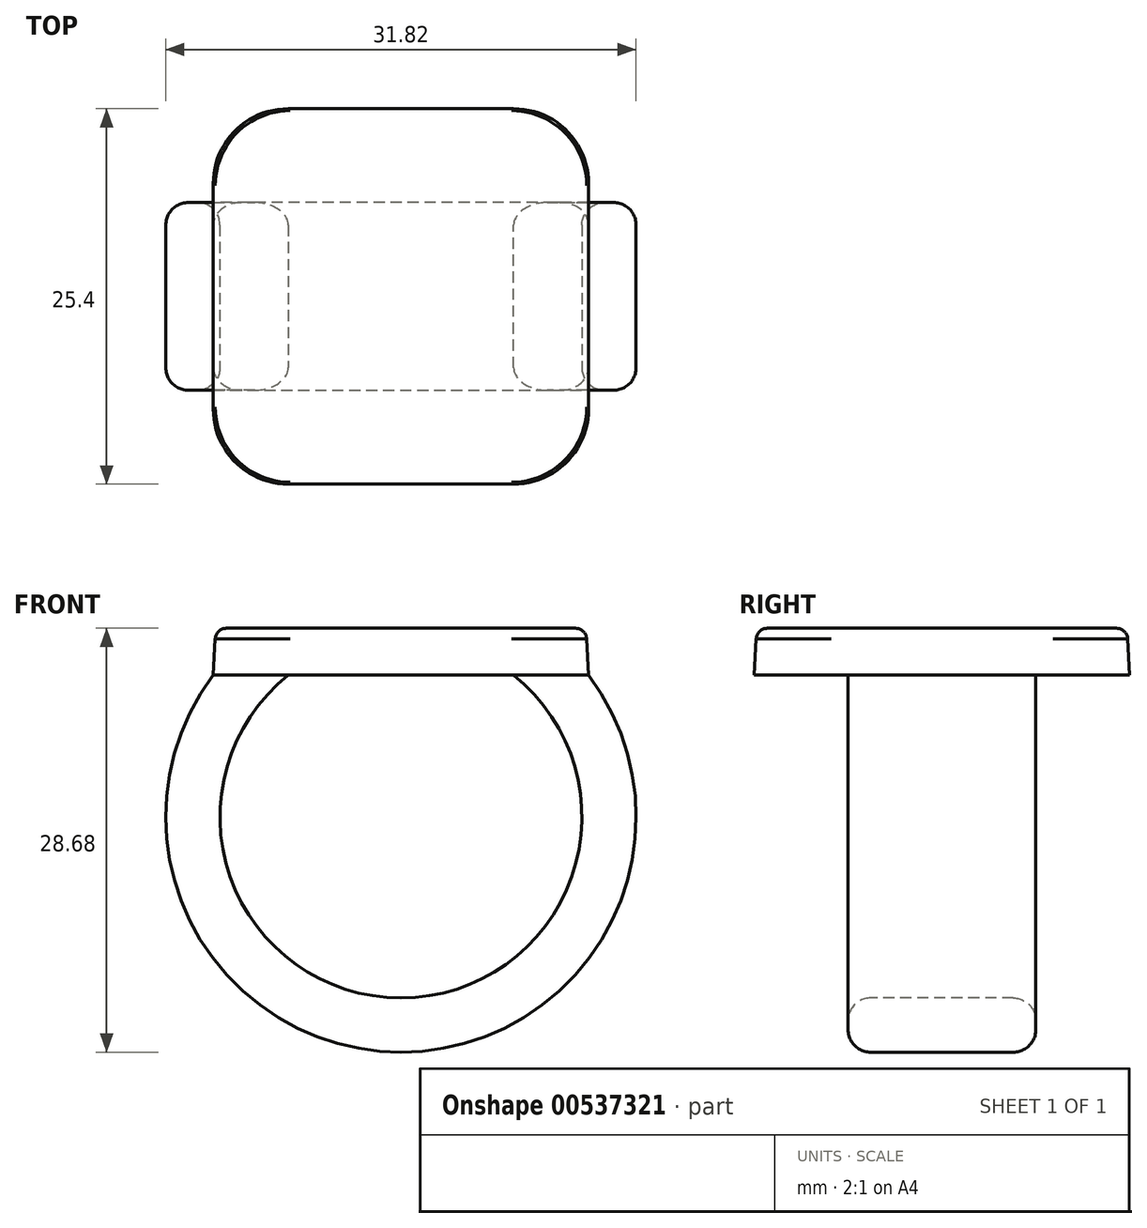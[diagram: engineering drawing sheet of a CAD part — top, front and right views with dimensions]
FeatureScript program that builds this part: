
annotation { "Feature Type Name" : "Feature", "Feature Type Description" : "" }
export const myFeature = defineFeature(function(context is Context, id is Id, definition is map)
    precondition{}
    {
        {
            var Q0;
            Q0=qCreatedBy(makeId("Top.planeOp"),FACE);
            var sketch = newSketch(context, id + "F0", { "sketchPlane" : qUnion([Q0])});
            skLineSegment(sketch, "E0.bottom", {"start": v(12.7, -12.7) * mm, "end": v(-12.7, -12.7) * mm});
            skLineSegment(sketch, "E0.top", {"start": v(12.7, 12.7) * mm, "end": v(-12.7, 12.7) * mm});
            skLineSegment(sketch, "E0.left", {"start": v(12.7, -12.7) * mm, "end": v(12.7, 12.7) * mm});
            skLineSegment(sketch, "E0.right", {"start": v(-12.7, -12.7) * mm, "end": v(-12.7, 12.7) * mm});
            skPoint(sketch, "E0.middle", {"position": v(0, 0) * mm});
            skSolve(sketch);
        }
        {
            var Q0;
            Q0 = qSketchRegion(id + "F0", true);
            extrude(context, id + "F1", {"entities" : qUnion([Q0]), "depth" : 3.17 * mm, "offsetDistance" : 25.4 * mm, "hasDraft" : true, "draftAngle" : 3 * degree, "draftPullDirection" : true});
        }
        {
            var Q0;
            Q0=qCreatedBy(makeId("Front.planeOp"),FACE);
            var sketch = newSketch(context, id + "F2", { "sketchPlane" : qUnion([Q0])});
            skArc(sketch, "E1", {"start": v(-10.16, 0) * mm, "mid": v(0, -23.56) * mm, "end": v(10.16, 0) * mm});
            skSolve(sketch);
        }
        {
            var Q0;
            Q0=makeQuery(id+"F1.opExtrude","CAP_FACE",FACE,{"disambiguationData":[OSD([sQuery(id+"F0.wireOp",EDGE,"E0.bottom"),sQuery(id+"F0.wireOp",EDGE,"E0.top"),sQuery(id+"F0.wireOp",EDGE,"E0.left"),sQuery(id+"F0.wireOp",EDGE,"E0.right")])],"isStart":true});
            var sketch = newSketch(context, id + "F3", { "sketchPlane" : qUnion([Q0])});
            skLineSegment(sketch, "E2.bottom", {"start": v(-7.62, -6.35) * mm, "end": v(-12.7, -6.35) * mm});
            skLineSegment(sketch, "E2.top", {"start": v(-7.62, 6.35) * mm, "end": v(-12.7, 6.35) * mm});
            skLineSegment(sketch, "E2.left", {"start": v(-7.62, -6.35) * mm, "end": v(-7.62, 6.35) * mm});
            skLineSegment(sketch, "E2.right", {"start": v(-12.7, -6.35) * mm, "end": v(-12.7, 6.35) * mm});
            skPoint(sketch, "E2.middle", {"position": v(-10.16, 0) * mm});
            skSolve(sketch);
        }
        {
            var Q0;
            Q0 = qSketchRegion(id + "F3", true);
            var Q1;
            Q1 = qConstructionFilter(qBodyType(qCreatedBy(id + "F2" ,EDGE), BodyType.WIRE), ConstructionObject.NO);
            sweep(context, id + "F4", {"operationType" : NewBodyOperationType.ADD, "profiles" : qUnion([Q0]), "path" : qUnion([Q1])});
        }
        {
            var Q0;
            Q0=qCreatedBy(makeId("Front.planeOp"),FACE);
            var sketch = newSketch(context, id + "F5", { "sketchPlane" : qUnion([Q0])});
            skLineSegment(sketch, "E3.0", {"start": v(12.7, 0) * mm, "end": v(7.62, 0) * mm});
            skLineSegment(sketch, "E3.1", {"start": v(10.01, -2.54) * mm, "end": v(10.16, 0) * mm});
            skArc(sketch, "E3.2", {"start": v(10.01, -2.54) * mm, "mid": v(8.9, -1.18) * mm, "end": v(7.62, 0) * mm});
            skPoint(sketch, "E4.orphan", {"position": v(-7.62, 0) * mm});
            skPoint(sketch, "E5.trimOffspring.end.orphan", {"position": v(-12.7, 0) * mm});
            skSolve(sketch);
        }
        {
            var Q0;
            Q0 = qSketchRegion(id + "F5", true);
            var Q1;
            Q1=makeQuery(id+"F4.opSweep","SWEPT_FACE",FACE,{"disambiguationData":[OSD([sQuery(id+"F2.wireOp",EDGE,"E1"),sQuery(id+"F3.wireOp",EDGE,"E2.top")])]});
            var Q2;
            Q2=makeQuery(id+"F4.opSweep","SWEPT_FACE",FACE,{"disambiguationData":[OSD([sQuery(id+"F2.wireOp",EDGE,"E1"),sQuery(id+"F3.wireOp",EDGE,"E2.bottom")])]});
            extrude(context, id + "F6", {"entities" : qUnion([Q0]), "operationType" : NewBodyOperationType.ADD, "endBound" : BoundingType.UP_TO_SURFACE, "depth" : 25.4 * mm, "endBoundEntityFace" : qUnion([Q1]), "offsetDistance" : 25.4 * mm, "hasSecondDirection" : true, "secondDirectionBound" : SecondDirectionBoundingType.UP_TO_SURFACE, "secondDirectionOppositeDirection" : true, "secondDirectionDepth" : 25.4 * mm, "secondDirectionBoundEntityFace" : qUnion([Q2])});
        }
        {
            var Q0;
            Q0=makeQuery(id+"F1.opExtrude","SWEPT_EDGE",EDGE,{"disambiguationData":[OSD([sQuery(id+"F0.wireOp",EDGE,"E0.top"),sQuery(id+"F0.wireOp",EDGE,"E0.right")])]});
            var Q1;
            Q1=makeQuery(id+"F1.opExtrude","SWEPT_EDGE",EDGE,{"disambiguationData":[OSD([sQuery(id+"F0.wireOp",EDGE,"E0.top"),sQuery(id+"F0.wireOp",EDGE,"E0.left")])]});
            var Q2;
            Q2=makeQuery(id+"F1.opExtrude","SWEPT_EDGE",EDGE,{"disambiguationData":[OSD([sQuery(id+"F0.wireOp",EDGE,"E0.bottom"),sQuery(id+"F0.wireOp",EDGE,"E0.left")])]});
            var Q3;
            Q3=makeQuery(id+"F1.opExtrude","SWEPT_EDGE",EDGE,{"disambiguationData":[OSD([sQuery(id+"F0.wireOp",EDGE,"E0.bottom"),sQuery(id+"F0.wireOp",EDGE,"E0.right")])]});
            fillet(context, id + "F7", {"entities" : qUnion([Q0, Q1, Q2, Q3]), "radius" : 5.08 * mm, "tangentPropagation" : true, "allowEdgeOverflow" : false});
        }
        {
            var Q0;
            {var subQ0=sQuery(id+"F3.wireOp",EDGE,"E2.top");var subQ1=sQuery(id+"F2.wireOp",EDGE,"E1");Q0=makeQuery(id+"F6.boolean.opBoolean","MERGE",EDGE,{"derivedFrom":[makeQuery(id+"F4.opSweep","SWEPT_EDGE",EDGE,{"disambiguationData":[OSD([subQ1,subQ0,sQuery(id+"F3.wireOp",EDGE,"E2.left")])]}),makeQuery(id+"F6.opExtrude","TWEAK_EDGE",EDGE,{"derivedFrom":[makeQuery(id+"F4.opSweep","SWEPT_FACE",FACE,{"disambiguationData":[OSD([subQ1,subQ0])]}),makeQuery(id+"F5.imprint","IMPRINT",EDGE,{"derivedFrom":sQuery(id+"F5.wireOp",EDGE,"E3.2")})]})]});}
            var Q1;
            Q1=makeQuery(id+"F4.opSweep","SWEPT_EDGE",EDGE,{"disambiguationData":[OSD([sQuery(id+"F0.wireOp",EDGE,"E0.right"),sQuery(id+"F2.wireOp",EDGE,"E1"),sQuery(id+"F3.wireOp",EDGE,"E2.top"),sQuery(id+"F3.wireOp",EDGE,"E2.right")])]});
            var Q2;
            Q2=makeQuery(id+"F4.opSweep","SWEPT_EDGE",EDGE,{"disambiguationData":[OSD([sQuery(id+"F0.wireOp",EDGE,"E0.right"),sQuery(id+"F2.wireOp",EDGE,"E1"),sQuery(id+"F3.wireOp",EDGE,"E2.bottom"),sQuery(id+"F3.wireOp",EDGE,"E2.right")])]});
            var Q3;
            {var subQ0=sQuery(id+"F3.wireOp",EDGE,"E2.bottom");var subQ1=sQuery(id+"F2.wireOp",EDGE,"E1");Q3=makeQuery(id+"F6.boolean.opBoolean","MERGE",EDGE,{"derivedFrom":[makeQuery(id+"F4.opSweep","SWEPT_EDGE",EDGE,{"disambiguationData":[OSD([subQ1,subQ0,sQuery(id+"F3.wireOp",EDGE,"E2.left")])]}),makeQuery(id+"F6.opExtrude","TWEAK_EDGE",EDGE,{"derivedFrom":[makeQuery(id+"F4.opSweep","SWEPT_FACE",FACE,{"disambiguationData":[OSD([subQ1,subQ0])]}),makeQuery(id+"F5.imprint","IMPRINT",EDGE,{"derivedFrom":sQuery(id+"F5.wireOp",EDGE,"E3.2")})]})]});}
            fillet(context, id + "F8", {"entities" : qUnion([Q0, Q1, Q2, Q3]), "radius" : 1.52 * mm, "tangentPropagation" : true, "allowEdgeOverflow" : false});
        }
        {
            var Q0;
            Q0=makeQuery(id+"F1.opExtrude","CAP_FACE",FACE,{"disambiguationData":[OSD([sQuery(id+"F0.wireOp",EDGE,"E0.bottom"),sQuery(id+"F0.wireOp",EDGE,"E0.top"),sQuery(id+"F0.wireOp",EDGE,"E0.left"),sQuery(id+"F0.wireOp",EDGE,"E0.right")])],"isStart":false});
            fillet(context, id + "F9", {"entities" : qUnion([Q0]), "radius" : 0.76 * mm, "tangentPropagation" : true, "allowEdgeOverflow" : false});
        }
    });
